# Revit family: 13_MAGIS40-33_F1A+FL-DX
name_source: partatom
category: Finestre
units: mm (PartAtom-declared; Revit-internal decimal feet)

## family parameters
Condiviso = No
Host = Muro
Numero OmniClass = 23.30.20.00
Punto di calcolo locali = Sì
Sempre verticale = Sì
Taglio con vuoti quando caricato = No
Titolo OmniClass = Windows

## types (3) — shared parameters
Chiusura muro = Per host
Costruzione analitica = <Nessuno>
EXTERNAL ALUMINUM FRAME/TELAIO ALLUMINIO ESTERNO = UNIFORM_ALUMINUM
GLASS WEIGHT/PESO VETRO = 30.00 kg/m²
HANDLE/MANIGLIA = UNIFORM_ALUMINUM
INTERIOR WOOD FRAME/TELAIO LEGNO INTERNO = UNIFORM_WOOD
MAXIMUM HEIGHT/ALTEZZA MASSIMA = 1800 mm  [stored 5.90551 ft]
MAXIMUM WIDTH/LARGHEZZA MASSIMA = 1800 mm  [stored 5.90551 ft]
MINIMUM HEIGHT/ALTEZZA MINIMA = 800 mm  [stored 2.62467 ft]
MINIMUM WIDTH/LARGHEZZA MINIMA  = 800 mm  [stored 2.62467 ft]
Modello = MAGIS40
PRODUCER WEBSITE/SITO WEB PRODUTTORE = www.uniform.it
PRODUCT WEBSITE/SITO WEB PRODOTTO = www.sistema-uni-one.it
WINDOW GLASS/VETRO FINESTRA = UNIFORM_GLASS

## per-type parameters (varying)
| type | Altezza | Altezza di default del davanzale | H | HANDLE HEIGHT/ALTEZZA MANIGLIA | LEFT HANDLE\MANIGLIA SINISTRA | Larghezza | MAX_DIMENSIONS_WARNING | RIGHT HANDLE\MANIGLIA DESTRA | Rw GLASS/Rw VETRO | Rw WINDOW/Rw FINESTRA | Ug GLASS/Ug VETRO | Uw WINDOW/Uw FINESTRA | W | W/2 | W/2 SX |
| ACOUSTICS | 1500 mm  [stored 4.92126 ft] | 800 mm  [stored 2.62467 ft] | 1500 mm  [stored 4.92126 ft] | 800 mm  [stored 2.62467 ft] | No | 1000 mm  [stored 3.28084 ft] | No | Sì | 43 | 40 | 1.6 W/(m²·K) | 1.6 W/(m²·K) | 1000 mm  [stored 3.28084 ft] | 483 mm | 535 mm |
| THERMAL_PERFORMANCE | 1000 mm  [stored 3.28084 ft] | 500 mm  [stored 1.64042 ft] | 1000 mm  [stored 3.28084 ft] | 500 mm  [stored 1.64042 ft] | Sì | 1500 mm  [stored 4.92126 ft] | No | No | 0 | 0 | 0.5 W/(m²·K) | 1.1 W/(m²·K) | 1500 mm  [stored 4.92126 ft] | 733 mm | 785 mm |
| THERMAL | 1500 mm  [stored 4.92126 ft] | 800 mm  [stored 2.62467 ft] | 1500 mm  [stored 4.92126 ft] | 500 mm  [stored 1.64042 ft] | Sì | 2500 mm  [stored 8.2021 ft] | Sì | No | 0 | 0 | 1 W/(m²·K) | 1.4 W/(m²·K) | 1800 mm  [stored 5.90551 ft] | 883 mm | 935 mm |

note: [stored X ft] marks values corroborated as IEEE doubles in the binary element streams (Revit-internal decimal feet)
